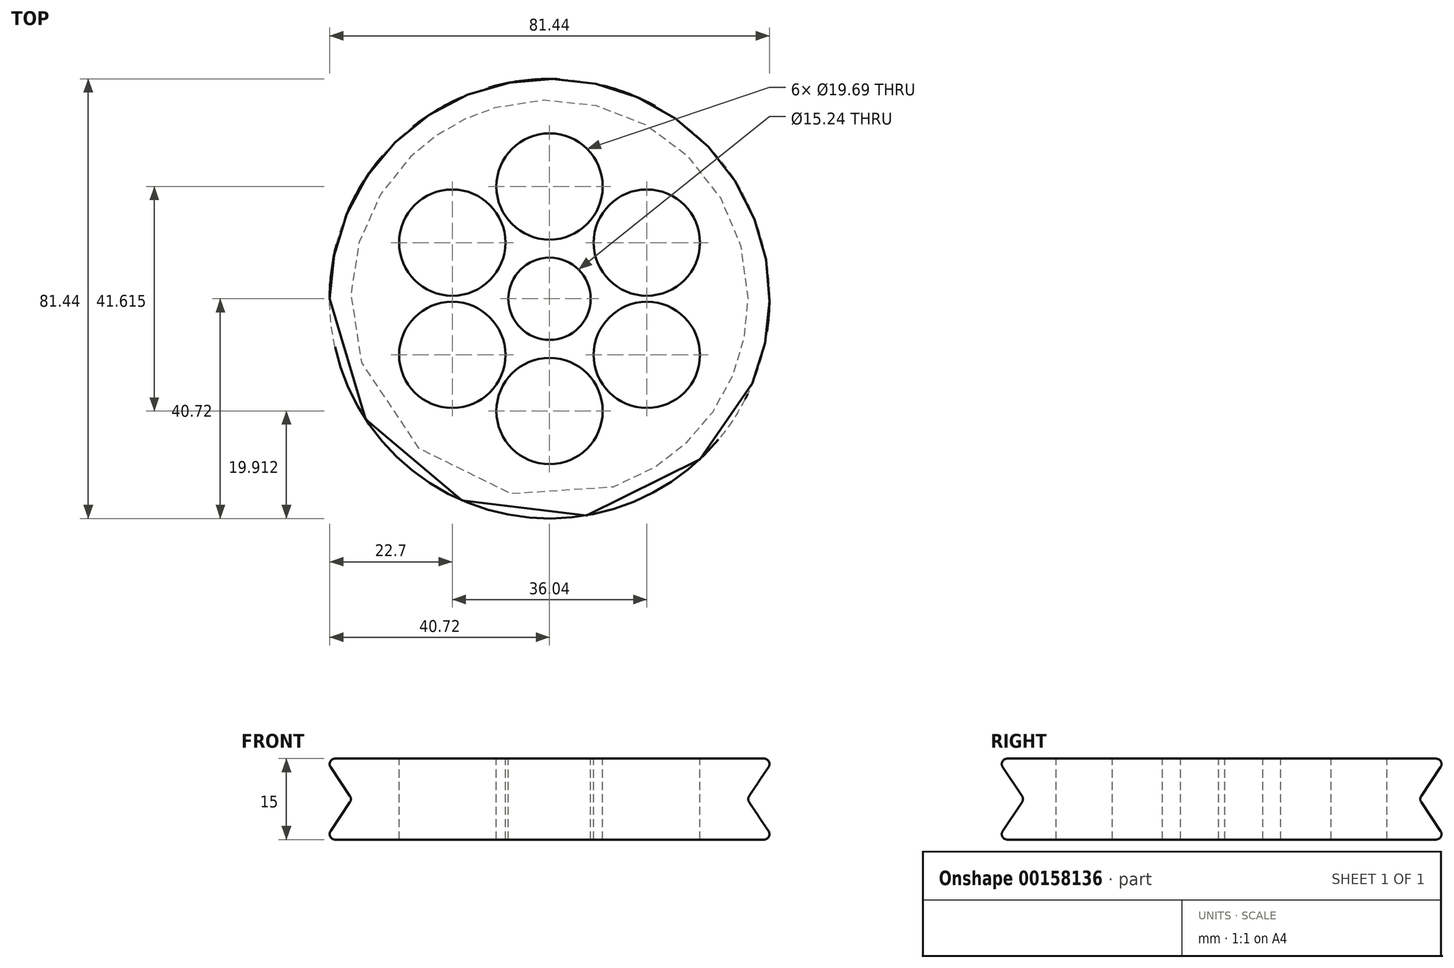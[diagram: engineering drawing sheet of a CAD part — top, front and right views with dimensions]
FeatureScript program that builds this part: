
annotation { "Feature Type Name" : "Feature", "Feature Type Description" : "" }
export const myFeature = defineFeature(function(context is Context, id is Id, definition is map)
    precondition{}
    {
        {
            var Q0;
            Q0=qCreatedBy(makeId("Front.planeOp"),FACE);
            var sketch = newSketch(context, id + "F0", { "sketchPlane" : qUnion([Q0])});
            skLineSegment(sketch, "E0", {"start": v(0, 7.5) * mm, "end": v(0, -7.5) * mm});
            skLineSegment(sketch, "E1", {"start": v(0, -7.5) * mm, "end": v(41.6, -7.5) * mm});
            skLineSegment(sketch, "E2", {"start": v(41.6, -7.5) * mm, "end": v(36.96, -0.55) * mm});
            skLineSegment(sketch, "E3", {"start": v(36.96, 0.55) * mm, "end": v(41.6, 7.5) * mm});
            skLineSegment(sketch, "E4", {"start": v(41.6, 7.5) * mm, "end": v(0, 7.5) * mm});
            skPoint(sketch, "E5.visualSharp", {"position": v(36.6, 0) * mm});
            skArc(sketch, "E5.filletArc", {"start": v(36.96, 0.55) * mm, "mid": v(36.8, 0) * mm, "end": v(36.96, -0.55) * mm});
            skSolve(sketch);
        }
        {
            var Q0;
            Q0 = qSketchRegion(id + "F0", true);
            var Q1;
            Q1=sQuery(id+"F0.wireOp",EDGE,"E0");
            revolve(context, id + "F1", {"entities" : qUnion([Q0]), "axis" : qUnion([Q1]), "revolveType" : RevolveType.FULL});
        }
        {
            var Q0;
            Q0=makeQuery(id+"F1.opRevolve","SWEPT_EDGE",EDGE,{"disambiguationData":[OSD([sQuery(id+"F0.wireOp",EDGE,"E3"),sQuery(id+"F0.wireOp",EDGE,"E4")])]});
            var Q1;
            Q1=makeQuery(id+"F1.opRevolve","SWEPT_EDGE",EDGE,{"disambiguationData":[OSD([sQuery(id+"F0.wireOp",EDGE,"E1"),sQuery(id+"F0.wireOp",EDGE,"E2")])]});
            fillet(context, id + "F2", {"entities" : qUnion([Q0, Q1]), "radius" : 1 * mm, "tangentPropagation" : true, "allowEdgeOverflow" : false});
        }
        {
            var Q0;
            Q0=qCreatedBy(makeId("Top.planeOp"),FACE);
            var sketch = newSketch(context, id + "F3", { "sketchPlane" : qUnion([Q0])});
            skCircle(sketch, "E6", {"center": v(0, 0) * mm, "radius": 7.62 * mm});
            skCircle(sketch, "E7", {"center": v(0, 0) * mm, "radius": 20.8 * mm, "construction": true});
            skCircle(sketch, "E8", {"center": v(0, 20.8) * mm, "radius": 9.84 * mm});
            skCircle(sketch, "E9.1.0", {"center": v(-18.02, 10.4) * mm, "radius": 9.84 * mm});
            skCircle(sketch, "E9.2.0", {"center": v(-18.02, -10.4) * mm, "radius": 9.84 * mm});
            skCircle(sketch, "E9.3.0", {"center": v(0, -20.8) * mm, "radius": 9.84 * mm});
            skCircle(sketch, "E9.4.0", {"center": v(18.02, -10.4) * mm, "radius": 9.84 * mm});
            skCircle(sketch, "E9.5.0", {"center": v(18.02, 10.4) * mm, "radius": 9.84 * mm});
            skPoint(sketch, "E10", {"position": v(0, 30.65) * mm});
            skPoint(sketch, "E11", {"position": v(0, 40.56) * mm});
            skSolve(sketch);
        }
        {
            var Q0;
            Q0 = qSketchRegion(id + "F3", true);
            extrude(context, id + "F4", {"entities" : qUnion([Q0]), "operationType" : NewBodyOperationType.REMOVE, "endBound" : BoundingType.THROUGH_ALL, "oppositeDirection" : true, "depth" : 25.4 * mm, "hasSecondDirection" : true, "secondDirectionBound" : SecondDirectionBoundingType.THROUGH_ALL, "secondDirectionOppositeDirection" : false, "secondDirectionDepth" : 25.4 * mm});
        }
    });
